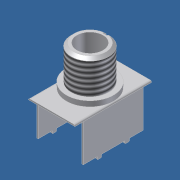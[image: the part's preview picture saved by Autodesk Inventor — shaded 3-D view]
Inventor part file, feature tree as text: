
AUTODESK INVENTOR PART (.ipt)
format: ipt  version: 2014 (Build 180170000, 170)  size: 185,344 bytes
history: native  units: in
note: dims shown in document units (in); Inventor stores cm internally (conversion verified against a paired STEP export)
features: other x35, sketch x5, extrude x3, revolve x2, thread x1
ambient origin geometry x8: Origin, YZ Plane, XZ Plane, XY Plane, X Axis, Y Axis, Z Axis, Center Point
bodies: Solid1 (feature_tree)
feature tree (46):
  extrude  "Extrusion1"  Depth=0.311in TaperAngle=0.0deg
  extrude  "Extrusion2"  Depth=0.225in TaperAngle=0.0deg
  revolve  "Revolution1"  Angle=360.0deg
  thread  "Thread1"  [1 undecoded]
  extrude  "Extrusion3"  [1 undecoded]
  revolve  "Revolution2"  [1 undecoded]
  other  "1_XY"
  other  "1_YZ"
  other  "1_ZX"
  other  "1_X"
  other  "1_Y"
  other  "1_Z"
  other  "1_Center"
  other  "2_XY"
  other  "2_YZ"
  other  "2_ZX"
  other  "2_X"
  other  "2_Y"
  other  "2_Z"
  other  "2_Center"
  other  "3_XY"
  other  "3_YZ"
  other  "3_ZX"
  other  "3_X"
  other  "3_Y"
  other  "3_Z"
  other  "3_Center"
  other  "4_XY"
  other  "4_YZ"
  other  "4_ZX"
  other  "4_X"
  other  "4_Y"
  other  "4_Z"
  other  "4_Center"
  other  "to_base_XY"
  other  "to_base_YZ"
  other  "to_base_ZX"
  other  "to_base_X"
  other  "to_base_Y"
  other  "to_base_Z"
  other  "to_base_Center"
  sketch  "Sketch_1"  dims[d0=0.512in d1=0.0in d2=0.311in d3=0.0in]
  sketch  "Sketch_2"  dims[d7=0.308in d8=0.0in d9=360.0deg]
  sketch  "Sketch_6"
  sketch  "Sketch_8"
  sketch  "Sketch_10_ALT_Drilling_1"  dims[d4=360.0deg d5=0.225in d6=0.0in]
note: 3 required parameter values undecoded (feature->parameter linkage not recoverable at this tier; creation-order binding heuristic only, values carry confidence <= 0.55)
